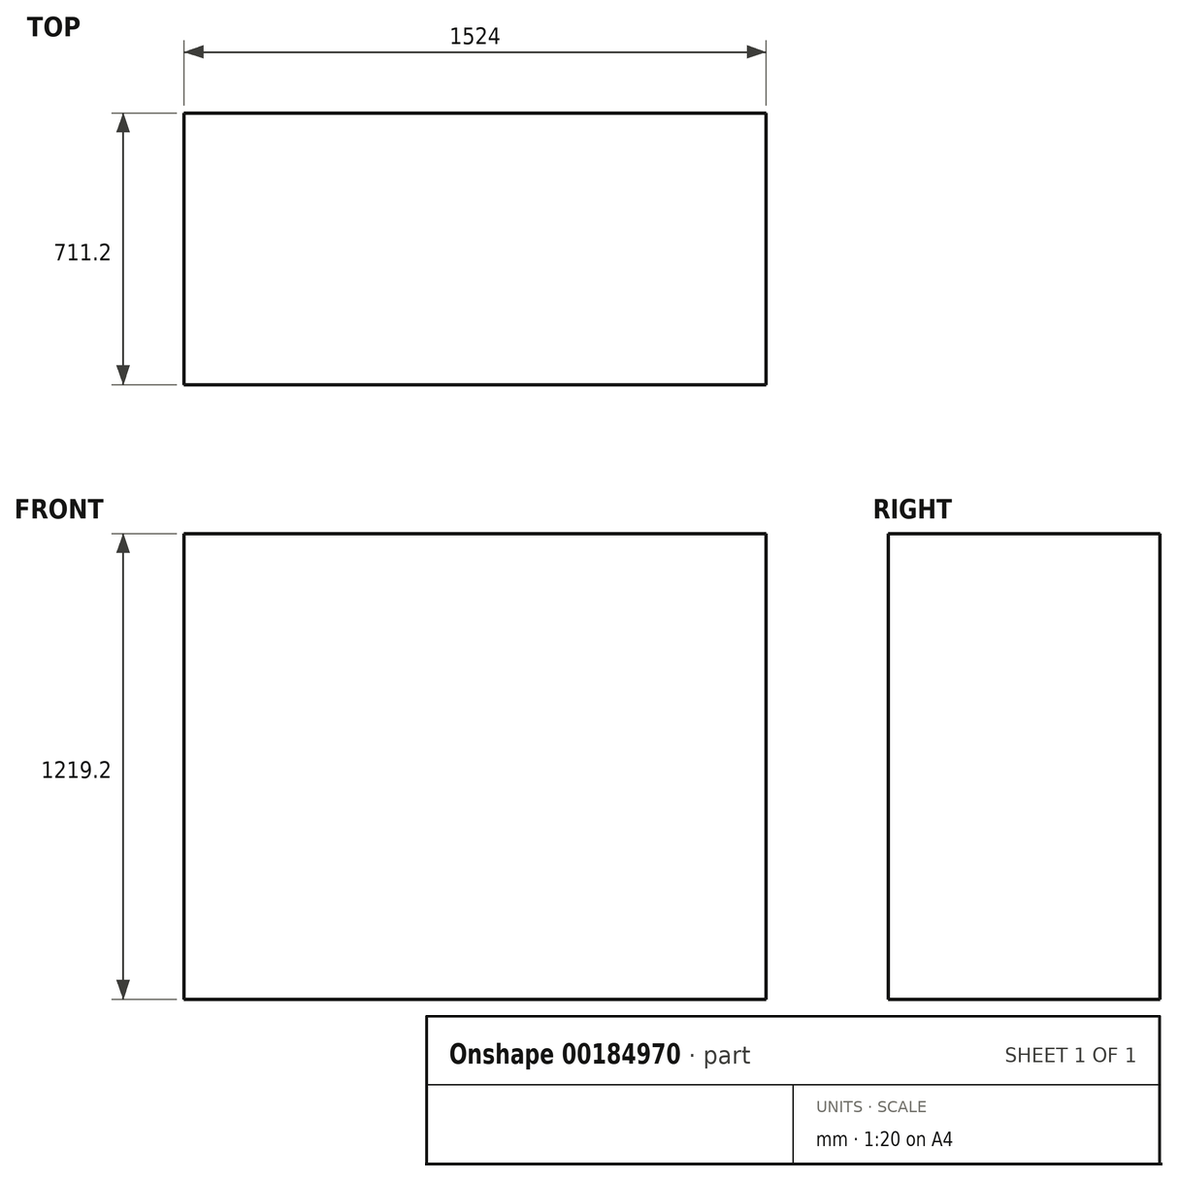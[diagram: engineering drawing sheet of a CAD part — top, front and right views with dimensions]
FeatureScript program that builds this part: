
annotation { "Feature Type Name" : "Feature", "Feature Type Description" : "" }
export const myFeature = defineFeature(function(context is Context, id is Id, definition is map)
    precondition{}
    {
        {
            var Q0;
            Q0=qCreatedBy(makeId("Top.planeOp"),FACE);
            var sketch = newSketch(context, id + "F0", { "sketchPlane" : qUnion([Q0])});
            skLineSegment(sketch, "E0.bottom", {"start": v(762, 355.6) * mm, "end": v(-762, 355.6) * mm});
            skLineSegment(sketch, "E0.top", {"start": v(762, -355.6) * mm, "end": v(-762, -355.6) * mm});
            skLineSegment(sketch, "E0.left", {"start": v(762, 355.6) * mm, "end": v(762, -355.6) * mm});
            skLineSegment(sketch, "E0.right", {"start": v(-762, 355.6) * mm, "end": v(-762, -355.6) * mm});
            skPoint(sketch, "E0.middle", {"position": v(0, 0) * mm});
            skSolve(sketch);
        }
        {
            var Q0;
            Q0=makeQuery(id+"F0.imprint","IMPRINT",FACE,{"disambiguationData":[TD([[makeQuery(id+"F0.imprint","IMPRINT",EDGE,{"derivedFrom":sQuery(id+"F0.wireOp",EDGE,"E0.bottom")}),1.0]])]});
            extrude(context, id + "F1", {"entities" : qUnion([Q0]), "depth" : 1219.2 * mm});
        }
    });
